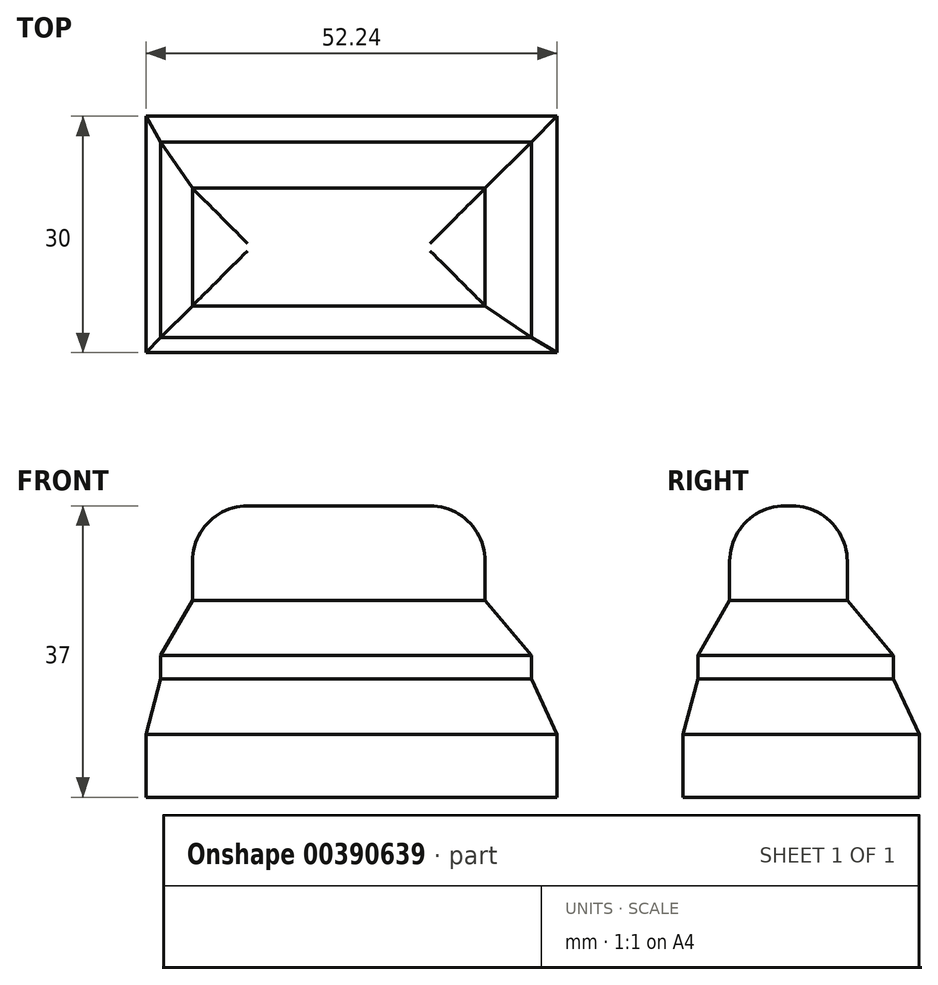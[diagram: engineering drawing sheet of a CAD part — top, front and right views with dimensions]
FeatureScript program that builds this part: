
annotation { "Feature Type Name" : "Feature", "Feature Type Description" : "" }
export const myFeature = defineFeature(function(context is Context, id is Id, definition is map)
    precondition{}
    {
        {
            var Q0;
            Q0=qCreatedBy(makeId("Top.planeOp"),FACE);
            var sketch = newSketch(context, id + "F0", { "sketchPlane" : qUnion([Q0])});
            skLineSegment(sketch, "E0.bottom", {"start": v(-0.67, 5.9) * mm, "end": v(-52.91, 5.9) * mm});
            skLineSegment(sketch, "E0.top", {"start": v(-0.67, 35.9) * mm, "end": v(-52.91, 35.9) * mm});
            skLineSegment(sketch, "E0.left", {"start": v(-0.67, 5.9) * mm, "end": v(-0.67, 35.9) * mm});
            skLineSegment(sketch, "E0.right", {"start": v(-52.91, 5.9) * mm, "end": v(-52.91, 35.9) * mm});
            skSolve(sketch);
        }
        {
            var Q0;
            Q0=makeQuery(id+"F0.imprint","IMPRINT",FACE,{"disambiguationData":[TD([[makeQuery(id+"F0.imprint","IMPRINT",EDGE,{"derivedFrom":sQuery(id+"F0.wireOp",EDGE,"E0.bottom")}),-1.0]])]});
            extrude(context, id + "F1", {"entities" : qUnion([Q0]), "depth" : 15 * mm});
        }
        {
            var Q0;
            Q0=makeQuery(id+"F1.opExtrude","CAP_EDGE",EDGE,{"disambiguationData":[OSD([sQuery(id+"F0.wireOp",EDGE,"E0.right")])],"isStart":false});
            var Q1;
            Q1=makeQuery(id+"F1.opExtrude","CAP_EDGE",EDGE,{"disambiguationData":[OSD([sQuery(id+"F0.wireOp",EDGE,"E0.bottom")])],"isStart":false});
            chamfer(context, id + "F2", {"entities" : qUnion([Q0, Q1]), "chamferType" : ChamferType.OFFSET_ANGLE, "width" : 7 * mm, "oppositeDirection" : false, "angle" : 15 * degree, "tangentPropagation" : true});
        }
        {
            var Q0;
            Q0=makeQuery(id+"F1.opExtrude","CAP_EDGE",EDGE,{"disambiguationData":[OSD([sQuery(id+"F0.wireOp",EDGE,"E0.top")])],"isStart":false});
            var Q1;
            Q1=makeQuery(id+"F1.opExtrude","CAP_EDGE",EDGE,{"disambiguationData":[OSD([sQuery(id+"F0.wireOp",EDGE,"E0.left")])],"isStart":false});
            chamfer(context, id + "F3", {"entities" : qUnion([Q0, Q1]), "chamferType" : ChamferType.OFFSET_ANGLE, "width" : 7 * mm, "oppositeDirection" : true, "angle" : 25 * degree});
        }
        {
            var Q0;
            Q0=makeQuery(id+"F1.opExtrude","CAP_FACE",FACE,{"disambiguationData":[OSD([sQuery(id+"F0.wireOp",EDGE,"E0.bottom"),sQuery(id+"F0.wireOp",EDGE,"E0.top"),sQuery(id+"F0.wireOp",EDGE,"E0.left"),sQuery(id+"F0.wireOp",EDGE,"E0.right")])],"isStart":false});
            extrude(context, id + "F4", {"entities" : qUnion([Q0]), "operationType" : NewBodyOperationType.ADD, "depth" : 10 * mm});
        }
        {
            var Q0;
            {var subQ0=sQuery(id+"F0.wireOp",EDGE,"E0.right");var subQ1=sQuery(id+"F0.wireOp",EDGE,"E0.left");var subQ2=sQuery(id+"F0.wireOp",EDGE,"E0.top");var subQ3=sQuery(id+"F0.wireOp",EDGE,"E0.bottom");Q0=makeQuery(id+"F4.opExtrude","CAP_EDGE",EDGE,{"disambiguationData":[OSD([subQ3,subQ2,subQ1,subQ0]),TDD([makeQuery(id+"F2.opChamfer","BLEND_EDGE",EDGE,{"blendedFrom":[makeQuery(id+"F1.opExtrude","CAP_EDGE",EDGE,{"disambiguationData":[OSD([subQ0])],"isStart":false}),makeQuery(id+"F1.opExtrude","CAP_FACE",FACE,{"disambiguationData":[OSD([subQ3,subQ2,subQ1,subQ0])],"isStart":false})],"blendedInto":[makeQuery(id+"F1.opExtrude","CAP_FACE",FACE,{"disambiguationData":[OSD([subQ3,subQ2,subQ1,subQ0])],"isStart":false})]})])],"isStart":false});}
            var Q1;
            {var subQ0=sQuery(id+"F0.wireOp",EDGE,"E0.right");var subQ1=sQuery(id+"F0.wireOp",EDGE,"E0.left");var subQ2=sQuery(id+"F0.wireOp",EDGE,"E0.top");var subQ3=sQuery(id+"F0.wireOp",EDGE,"E0.bottom");Q1=makeQuery(id+"F4.opExtrude","CAP_EDGE",EDGE,{"disambiguationData":[OSD([subQ3,subQ2,subQ1,subQ0]),TDD([makeQuery(id+"F2.opChamfer","BLEND_EDGE",EDGE,{"blendedFrom":[makeQuery(id+"F1.opExtrude","CAP_EDGE",EDGE,{"disambiguationData":[OSD([subQ3])],"isStart":false}),makeQuery(id+"F1.opExtrude","CAP_FACE",FACE,{"disambiguationData":[OSD([subQ3,subQ2,subQ1,subQ0])],"isStart":false})],"blendedInto":[makeQuery(id+"F1.opExtrude","CAP_FACE",FACE,{"disambiguationData":[OSD([subQ3,subQ2,subQ1,subQ0])],"isStart":false})]})])],"isStart":false});}
            chamfer(context, id + "F5", {"entities" : qUnion([Q0, Q1]), "chamferType" : ChamferType.OFFSET_ANGLE, "width" : 7 * mm, "oppositeDirection" : true, "angle" : 30 * degree, "tangentPropagation" : true});
        }
        {
            var Q0;
            {var subQ0=sQuery(id+"F0.wireOp",EDGE,"E0.right");var subQ1=sQuery(id+"F0.wireOp",EDGE,"E0.left");var subQ2=sQuery(id+"F0.wireOp",EDGE,"E0.top");var subQ3=sQuery(id+"F0.wireOp",EDGE,"E0.bottom");Q0=makeQuery(id+"F4.opExtrude","CAP_EDGE",EDGE,{"disambiguationData":[OSD([subQ3,subQ2,subQ1,subQ0]),TDD([makeQuery(id+"F3.opChamfer","BLEND_EDGE",EDGE,{"blendedFrom":[makeQuery(id+"F1.opExtrude","CAP_EDGE",EDGE,{"disambiguationData":[OSD([subQ2])],"isStart":false}),makeQuery(id+"F1.opExtrude","CAP_FACE",FACE,{"disambiguationData":[OSD([subQ3,subQ2,subQ1,subQ0])],"isStart":false})],"blendedInto":[makeQuery(id+"F1.opExtrude","CAP_FACE",FACE,{"disambiguationData":[OSD([subQ3,subQ2,subQ1,subQ0])],"isStart":false})]})])],"isStart":false});}
            var Q1;
            {var subQ0=sQuery(id+"F0.wireOp",EDGE,"E0.right");var subQ1=sQuery(id+"F0.wireOp",EDGE,"E0.left");var subQ2=sQuery(id+"F0.wireOp",EDGE,"E0.top");var subQ3=sQuery(id+"F0.wireOp",EDGE,"E0.bottom");Q1=makeQuery(id+"F4.opExtrude","CAP_EDGE",EDGE,{"disambiguationData":[OSD([subQ3,subQ2,subQ1,subQ0]),TDD([makeQuery(id+"F3.opChamfer","BLEND_EDGE",EDGE,{"blendedFrom":[makeQuery(id+"F1.opExtrude","CAP_EDGE",EDGE,{"disambiguationData":[OSD([subQ1])],"isStart":false}),makeQuery(id+"F1.opExtrude","CAP_FACE",FACE,{"disambiguationData":[OSD([subQ3,subQ2,subQ1,subQ0])],"isStart":false})],"blendedInto":[makeQuery(id+"F1.opExtrude","CAP_FACE",FACE,{"disambiguationData":[OSD([subQ3,subQ2,subQ1,subQ0])],"isStart":false})]})])],"isStart":false});}
            chamfer(context, id + "F6", {"entities" : qUnion([Q0, Q1]), "chamferType" : ChamferType.OFFSET_ANGLE, "width" : 7 * mm, "oppositeDirection" : true, "angle" : 40 * degree, "tangentPropagation" : true});
        }
        {
            var Q0;
            Q0=makeQuery(id+"F4.opExtrude","CAP_FACE",FACE,{"disambiguationData":[OSD([sQuery(id+"F0.wireOp",EDGE,"E0.bottom"),sQuery(id+"F0.wireOp",EDGE,"E0.top"),sQuery(id+"F0.wireOp",EDGE,"E0.left"),sQuery(id+"F0.wireOp",EDGE,"E0.right")])],"isStart":false});
            extrude(context, id + "F7", {"entities" : qUnion([Q0]), "operationType" : NewBodyOperationType.ADD, "depth" : 12 * mm});
        }
        {
            var Q0;
            Q0=makeQuery(id+"F7.opExtrude","CAP_FACE",FACE,{"disambiguationData":[OSD([sQuery(id+"F0.wireOp",EDGE,"E0.bottom"),sQuery(id+"F0.wireOp",EDGE,"E0.top"),sQuery(id+"F0.wireOp",EDGE,"E0.left"),sQuery(id+"F0.wireOp",EDGE,"E0.right")])],"isStart":false});
            fillet(context, id + "F8", {"entities" : qUnion([Q0]), "radius" : 7 * mm, "tangentPropagation" : true, "allowEdgeOverflow" : false});
        }
    });
